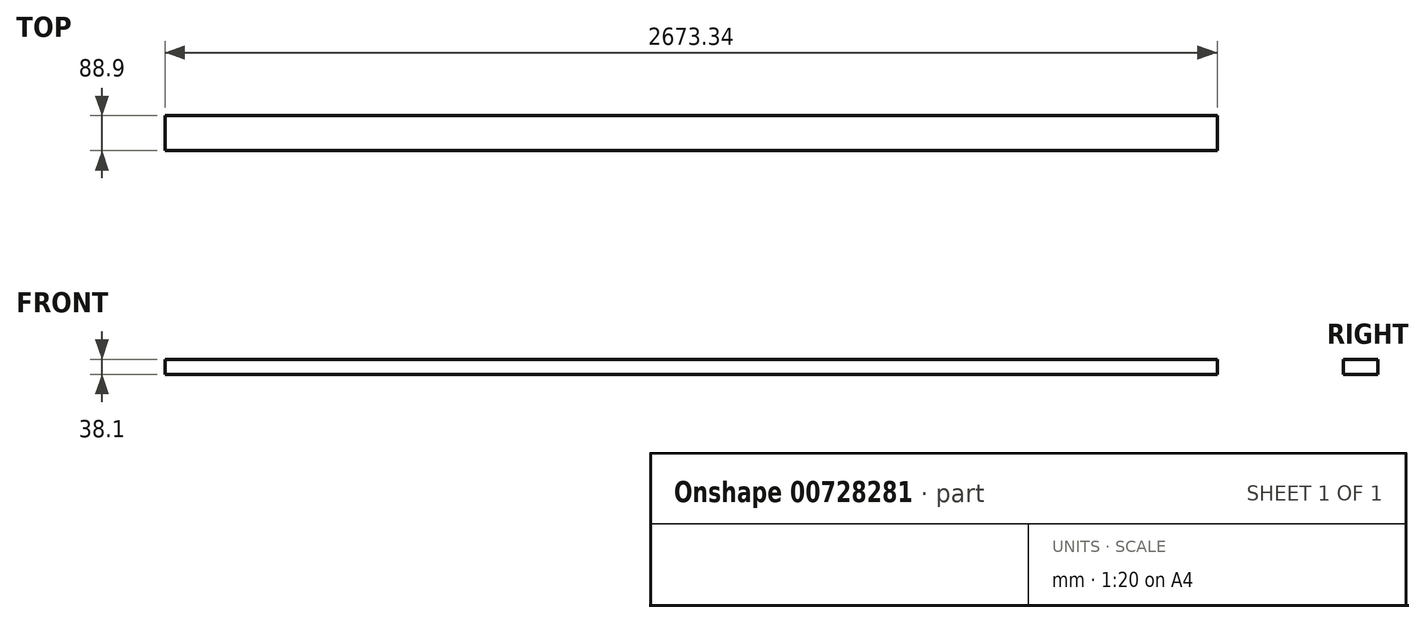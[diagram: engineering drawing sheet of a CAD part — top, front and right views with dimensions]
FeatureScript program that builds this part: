
annotation { "Feature Type Name" : "Feature", "Feature Type Description" : "" }
export const myFeature = defineFeature(function(context is Context, id is Id, definition is map)
    precondition{}
    {
        {
            var Q0;
            Q0=qCreatedBy(makeId("Top.planeOp"),FACE);
            var sketch = newSketch(context, id + "F0", { "sketchPlane" : qUnion([Q0])});
            skLineSegment(sketch, "E0.bottom", {"start": v(-1336.67, -44.45) * mm, "end": v(1336.67, -44.45) * mm});
            skLineSegment(sketch, "E0.top", {"start": v(-1336.67, 44.45) * mm, "end": v(1336.67, 44.45) * mm});
            skLineSegment(sketch, "E0.left", {"start": v(-1336.67, -44.45) * mm, "end": v(-1336.67, 44.45) * mm});
            skLineSegment(sketch, "E0.right", {"start": v(1336.67, -44.45) * mm, "end": v(1336.67, 44.45) * mm});
            skPoint(sketch, "E0.middle", {"position": v(0, 0) * mm});
            skSolve(sketch);
        }
        {
            var Q0;
            Q0=qSketchRegion(id+"F0",true);
            extrude(context, id + "F1", {"entities" : qUnion([Q0]), "depth" : 38.1 * mm, "offsetDistance" : 25.4 * mm});
        }
    });
